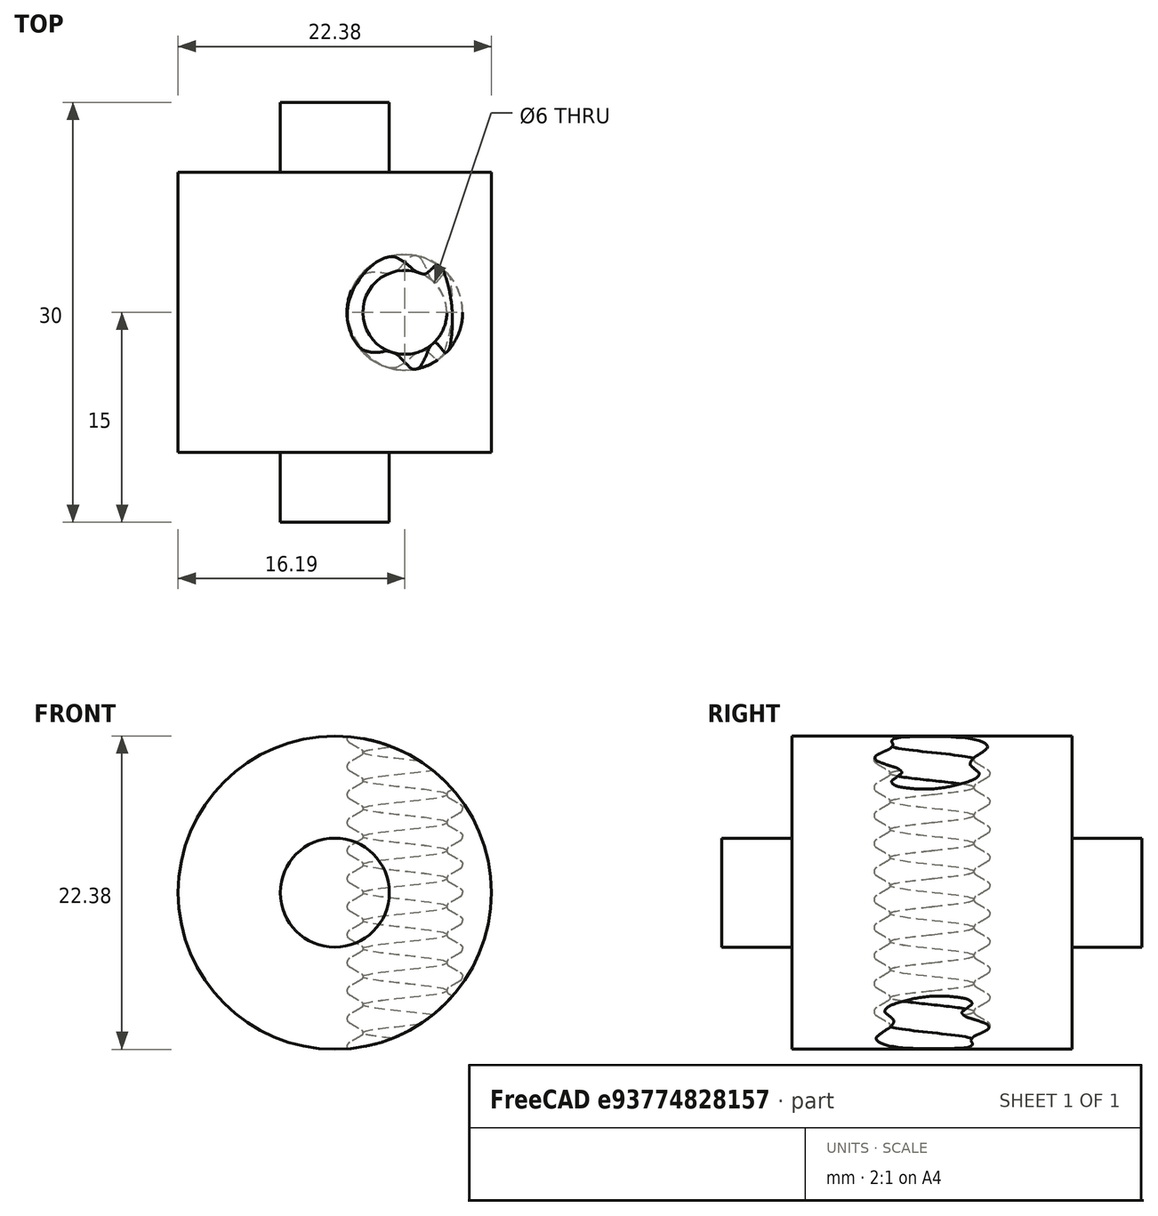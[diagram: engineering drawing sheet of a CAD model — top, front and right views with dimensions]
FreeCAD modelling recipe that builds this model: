
FCSTD DOCUMENT  (FreeCAD 1.0R39319 (Git))
Label: SubtractiveHelix
License: All rights reserved
LicenseURL: https://en.wikipedia.org/wiki/All_rights_reserved
objects: Sketcher::SketchObject×4, PartDesign::Pad×2, PartDesign::Pocket×1, PartDesign::SubtractiveHelix×1, PartDesign::Body×1
note: 21 computed .brp shape members not serialized (recipe doc carries the construction recipe); baked Part::Feature solids carry a one-line shape summary decoded from their .brp

FEATURE [Sketcher::SketchObject] Sketch
  ArcFitTolerance = 1e-06
  AttachmentSupport = -> [XZ_Plane]
  FullyConstrained = false
  MakeInternals = false
  MapMode = 5
  Placement = pos=(0,0,0) rot=(1,0,0;1.5708rad)
  sketch-geometry (1):
    g0: Circle CenterX=0 CenterY=0 CenterZ=0 NormalX=0 NormalY=0 NormalZ=1 AngleXU=0 Radius=3.89332
  constraints (1):
    c: Coincident(g0,g-1)
FEATURE [PartDesign::Pad] Pad
  Direction = (0,-1,2e-16)
  Length = 30
  Length2 = 10
  Midplane = true
  Placement = pos=(0,0,0) rot=(1,0,0;1.5708rad)
  Profile = -> Sketch
  ReferenceAxis = -> Sketch [N_Axis]
  Refine = true
  Suppressed = false
  Type = 0
FEATURE [Sketcher::SketchObject] Sketch001
  ArcFitTolerance = 1e-06
  AttachmentSupport = -> [XZ_Plane]
  FullyConstrained = false
  MakeInternals = false
  MapMode = 5
  Placement = pos=(0,0,0) rot=(1,0,0;1.5708rad)
  sketch-geometry (1):
    g0: Circle CenterX=0 CenterY=0 CenterZ=0 NormalX=0 NormalY=0 NormalZ=1 AngleXU=0 Radius=11.186
  constraints (1):
    c: Coincident(g0,g-1)
FEATURE [PartDesign::Pad] Pad001
  BaseFeature = -> Pad
  Direction = (0,-1,2e-16)
  Length = 20
  Length2 = 10
  Midplane = true
  Placement = pos=(0,0,0) rot=(1,0,0;1.5708rad)
  Profile = -> Sketch001
  ReferenceAxis = -> Sketch001 [N_Axis]
  Refine = true
  Suppressed = false
  Type = 0
FEATURE [Sketcher::SketchObject] Sketch002
  ArcFitTolerance = 1e-06
  AttachmentSupport = -> [XY_Plane]
  FullyConstrained = true
  MakeInternals = false
  MapMode = 5
  sketch-geometry (1):
    g0: Circle CenterX=5 CenterY=0 CenterZ=0 NormalX=0 NormalY=0 NormalZ=1 AngleXU=0 Radius=3
  constraints (3):
    c: PointOnObject(g0,g-1)
    c: Radius(g0) = 3
    c: DistanceX(g-1,g0) = 5
FEATURE [PartDesign::Pocket] Pocket
  BaseFeature = -> Pad001
  Direction = (0,0,-1)
  Length = 5
  Length2 = 5
  Midplane = true
  Placement = pos=(0,0,0) rot=(1,0,0;1.5708rad)
  Profile = -> Sketch002
  ReferenceAxis = -> Sketch002 [N_Axis]
  Refine = true
  Suppressed = false
  Type = 1
FEATURE [Sketcher::SketchObject] Sketch003
  ArcFitTolerance = 1e-06
  AttachmentOffset = pos=(5,-12,0) rot=(0,0,1;0rad)
  AttachmentSupport = -> [XZ_Plane]
  FullyConstrained = true
  MakeInternals = false
  MapMode = 5
  Placement = pos=(5,-2.7e-15,-12) rot=(1,0,0;1.5708rad)
  sketch-geometry (6):
    g0: LineSegment StartX=3.15 StartY=0.740192 StartZ=0 EndX=3.98205 EndY=0.259808 EndZ=0
    g1: ArcOfCircle CenterX=3.83205 CenterY=0 CenterZ=0 NormalX=0 NormalY=0 NormalZ=1 AngleXU=0 Radius=0.3 StartAngle=5.23599 EndAngle=7.33038
    g2: LineSegment StartX=3.98205 StartY=-0.259808 StartZ=0 EndX=3.15 EndY=-0.740192 EndZ=0
    g3: LineSegment StartX=3 StartY=-1 StartZ=0 EndX=3 EndY=1 EndZ=0
    g4: ArcOfCircle CenterX=3.3 CenterY=1 CenterZ=0 NormalX=0 NormalY=0 NormalZ=1 AngleXU=0 Radius=0.3 StartAngle=3.14159 EndAngle=4.18879
    g5: ArcOfCircle CenterX=3.3 CenterY=-1 CenterZ=0 NormalX=0 NormalY=0 NormalZ=1 AngleXU=0 Radius=0.3 StartAngle=2.0944 EndAngle=3.14159
  constraints (14):
    c: Tangent(g0,g1) = 1.5708
    c: Radius(g1) = 0.3
    c: PointOnObject(g1,g-1)
    c: Tangent(g1,g2) = 1.5708
    c: Angle(g0,g2) = 1.0472
    c: DistanceY(g3,g3) = 2
    c: Tangent(g5,g2) = -1.5708
    c: Tangent(g5,g3) = 1.5708
    c: Tangent(g4,g0) = -1.5708
    c: Tangent(g4,g3) = 1.5708
    c: Equal(g5,g4)
    c: Equal(g5,g1)
    c: Symmetric(g3,g3,g-1)
    c: DistanceX(g3) = 3
FEATURE [PartDesign::SubtractiveHelix] SubtractiveHelix
  Angle = 0
  Axis = (0,2e-16,1)
  Base = (5,-2.7e-15,-12)
  BaseFeature = -> Pocket
  Growth = 0
  HasBeenEdited = true
  Height = 24
  LeftHanded = false
  Mode = 0
  Outside = false
  Pitch = 2.001
  Placement = pos=(0,0,0) rot=(1,0,0;1.5708rad)
  Profile = -> Sketch003
  ReferenceAxis = -> Sketch003 [V_Axis]
  Refine = true
  Suppressed = false
  Tolerance = 0.1
  Turns = 11.994
FEATURE [PartDesign::Body] Body
  AllowCompound = false
  Group = -> [Sketch,Pad,Sketch001,Pad001,Sketch002,Pocket,Sketch003,SubtractiveHelix]
  Origin = -> Origin
  Tip = -> SubtractiveHelix
